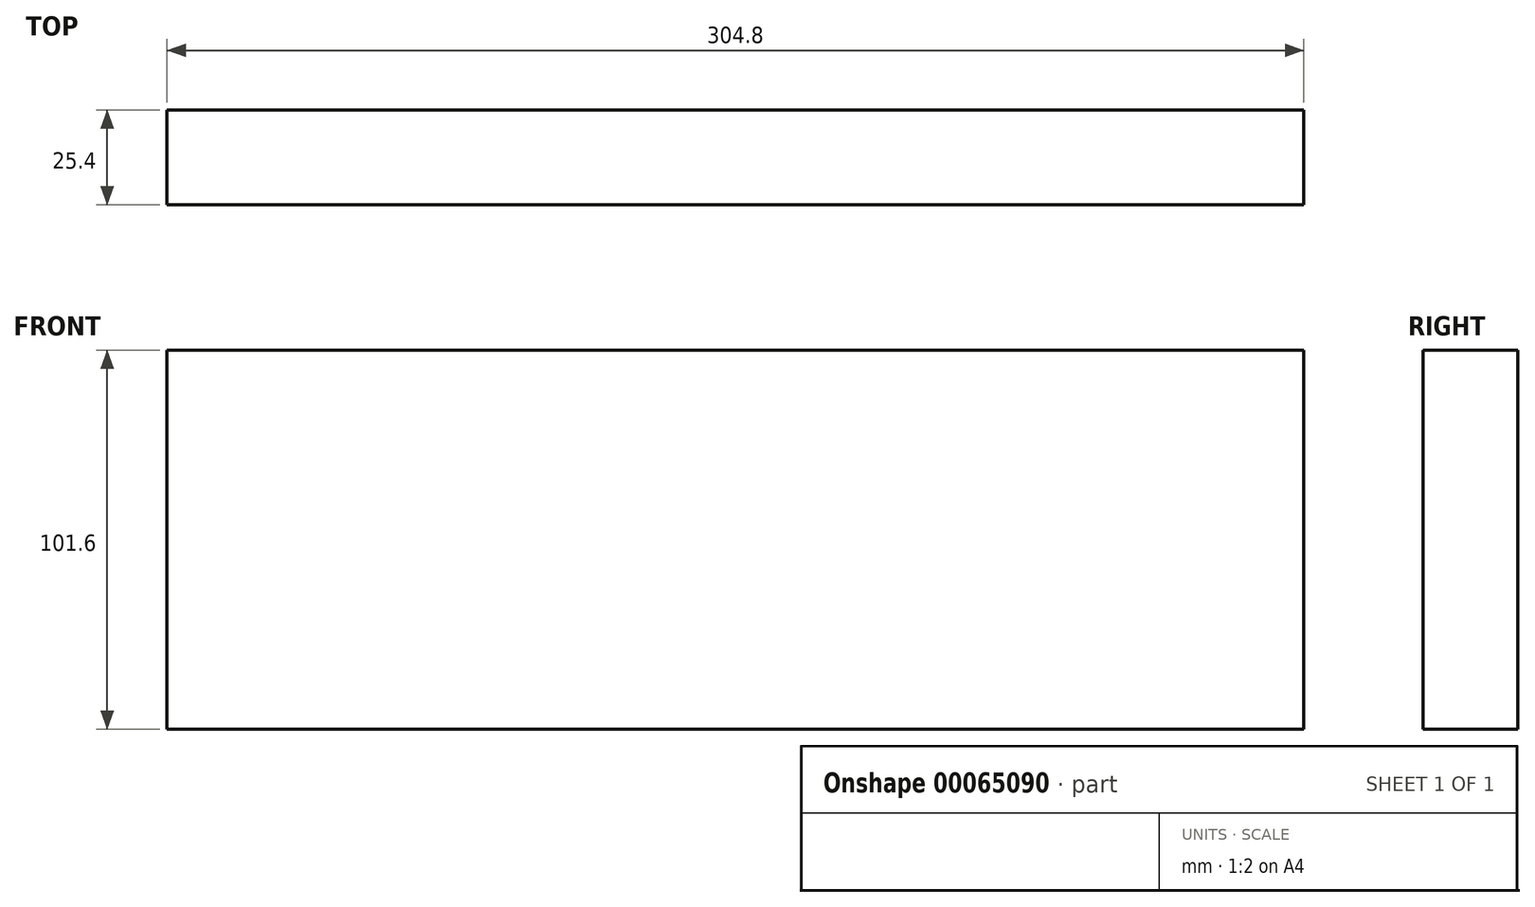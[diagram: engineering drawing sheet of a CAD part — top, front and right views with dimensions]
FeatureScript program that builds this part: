
annotation { "Feature Type Name" : "Feature", "Feature Type Description" : "" }
export const myFeature = defineFeature(function(context is Context, id is Id, definition is map)
    precondition{}
    {
        {
            var Q0;
            Q0=qCreatedBy(makeId("Front.planeOp"),FACE);
            var sketch = newSketch(context, id + "F0", { "sketchPlane" : qUnion([Q0])});
            skLineSegment(sketch, "E0.rect.bottom", {"start": v(152.4, 50.8) * mm, "end": v(-152.4, 50.8) * mm});
            skLineSegment(sketch, "E0.rect.top", {"start": v(152.4, -50.8) * mm, "end": v(-152.4, -50.8) * mm});
            skLineSegment(sketch, "E0.rect.left", {"start": v(152.4, 50.8) * mm, "end": v(152.4, -50.8) * mm});
            skLineSegment(sketch, "E0.rect.right", {"start": v(-152.4, 50.8) * mm, "end": v(-152.4, -50.8) * mm});
            skPoint(sketch, "E0.rect.middle", {"position": v(0, 0) * mm});
            skSolve(sketch);
        }
        {
            var Q0;
            Q0 = qSketchRegion(id + "F0", true);
            extrude(context, id + "F1", {"entities" : qUnion([Q0]), "depth" : 25.4 * mm});
        }
    });
